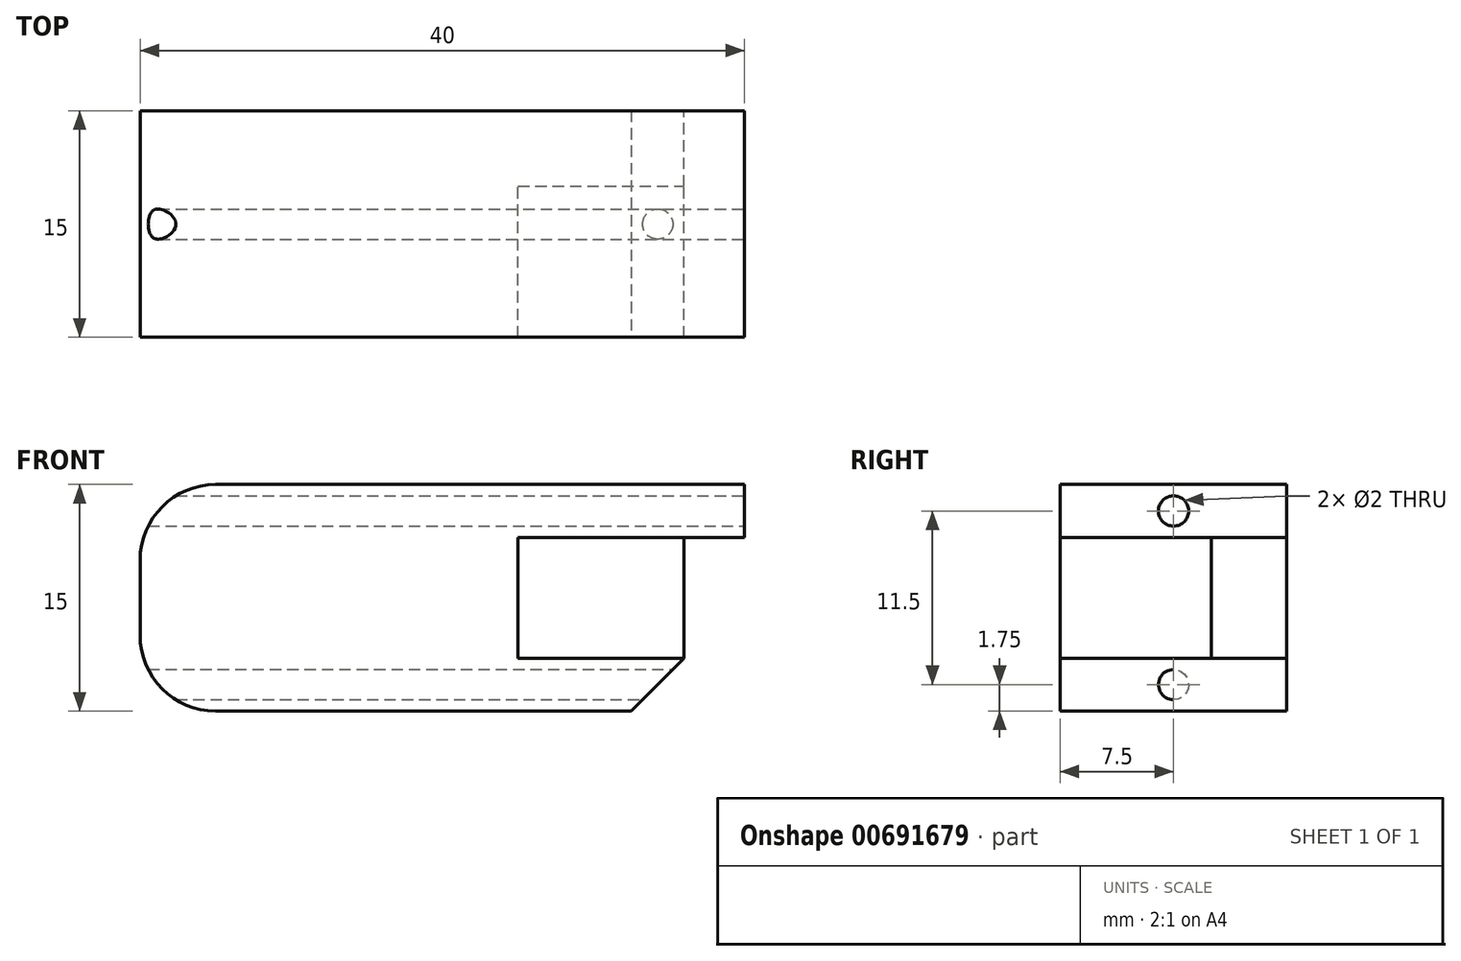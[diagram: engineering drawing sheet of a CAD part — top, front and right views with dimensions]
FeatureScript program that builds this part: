
annotation { "Feature Type Name" : "Feature", "Feature Type Description" : "" }
export const myFeature = defineFeature(function(context is Context, id is Id, definition is map)
    precondition{}
    {
        {
            var Q0;
            Q0=qCreatedBy(makeId("Front.planeOp"),FACE);
            var sketch = newSketch(context, id + "F0", { "sketchPlane" : qUnion([Q0])});
            skLineSegment(sketch, "E0.bottom", {"start": v(5, 4) * mm, "end": v(-5, 4) * mm});
            skLineSegment(sketch, "E0.top", {"start": v(5, -4) * mm, "end": v(-5, -4) * mm});
            skLineSegment(sketch, "E0.left", {"start": v(5, 4) * mm, "end": v(5, -4) * mm});
            skLineSegment(sketch, "E0.right", {"start": v(-5, 4) * mm, "end": v(-5, -4) * mm});
            skPoint(sketch, "E0.middle", {"position": v(0, 0) * mm});
            skLineSegment(sketch, "E1.bottom", {"start": v(-5, 4) * mm, "end": v(-20, 4) * mm});
            skLineSegment(sketch, "E1.top", {"start": v(-5, -4) * mm, "end": v(-20, -4) * mm});
            skLineSegment(sketch, "E1.right", {"start": v(-20, 4) * mm, "end": v(-20, -4) * mm});
            skLineSegment(sketch, "E2.bottom", {"start": v(5, 4) * mm, "end": v(20, 4) * mm});
            skLineSegment(sketch, "E2.top", {"start": v(5, -4) * mm, "end": v(20, -4) * mm});
            skLineSegment(sketch, "E2.right", {"start": v(20, 4) * mm, "end": v(20, -4) * mm});
            skLineSegment(sketch, "E3.bottom", {"start": v(-20, 4) * mm, "end": v(20, 4) * mm});
            skLineSegment(sketch, "E3.top", {"start": v(-20, 7.5) * mm, "end": v(20, 7.5) * mm});
            skLineSegment(sketch, "E3.left", {"start": v(-20, 4) * mm, "end": v(-20, 7.5) * mm});
            skLineSegment(sketch, "E3.right", {"start": v(20, 4) * mm, "end": v(20, 7.5) * mm});
            skLineSegment(sketch, "E4.bottom", {"start": v(-16, 0) * mm, "end": v(16, 0) * mm});
            skLineSegment(sketch, "E4.top", {"start": v(-16, -7.5) * mm, "end": v(16, -7.5) * mm});
            skLineSegment(sketch, "E4.left", {"start": v(-16, 0) * mm, "end": v(-16, -7.5) * mm});
            skLineSegment(sketch, "E4.right", {"start": v(16, 0) * mm, "end": v(16, -7.5) * mm});
            skLineSegment(sketch, "E5.bottom", {"start": v(5, 4) * mm, "end": v(16, 4) * mm});
            skLineSegment(sketch, "E5.top", {"start": v(5, -4) * mm, "end": v(16, -4) * mm});
            skLineSegment(sketch, "E5.right", {"start": v(16, 4) * mm, "end": v(16, -4) * mm});
            skLineSegment(sketch, "E6.bottom", {"start": v(-5, 4) * mm, "end": v(-16, 4) * mm});
            skLineSegment(sketch, "E6.top", {"start": v(-5, -4) * mm, "end": v(-16, -4) * mm});
            skLineSegment(sketch, "E6.right", {"start": v(-16, 4) * mm, "end": v(-16, -4) * mm});
            skLineSegment(sketch, "E7.bottom", {"start": v(-20, 7.5) * mm, "end": v(-5, 7.5) * mm});
            skLineSegment(sketch, "E7.top", {"start": v(-20, -7.5) * mm, "end": v(-5, -7.5) * mm});
            skLineSegment(sketch, "E7.left", {"start": v(-20, 7.5) * mm, "end": v(-20, -7.5) * mm});
            skLineSegment(sketch, "E7.right", {"start": v(-5, 7.5) * mm, "end": v(-5, -7.5) * mm});
            skSolve(sketch);
        }
        {
            var Q0;
            {var subQ4=sQuery(id+"F0.wireOp",EDGE,"E7.top");Q0=makeQuery(id+"F0.imprint","IMPRINT",FACE,{"disambiguationData":[TD([[makeQuery(id+"F0.imprint","IMPRINT",EDGE,{"derivedFrom":subQ4}),1.0]])]});}
            var Q1;
            {var subQ7=sQuery(id+"F0.wireOp",EDGE,"E0.top");Q1=makeQuery(id+"F0.imprint","IMPRINT",FACE,{"disambiguationData":[TD([[makeQuery(id+"F0.imprint","IMPRINT",EDGE,{"derivedFrom":subQ7}),1.0]])]});}
            var Q2;
            {var subQ0=sQuery(id+"F0.wireOp",EDGE,"E3.left");Q2=makeQuery(id+"F0.imprint","IMPRINT",FACE,{"disambiguationData":[TD([[makeQuery(id+"F0.imprint","IMPRINT",EDGE,{"derivedFrom":subQ0}),-1.0]])]});}
            var Q3;
            {var subQ0=sQuery(id+"F0.wireOp",EDGE,"E7.right");var subQ5=sQuery(id+"F0.wireOp",EDGE,"E4.top");var subQ6=makeQuery(id+"F0.imprint","INTERSECT",VERTEX,{"derivedFrom":[subQ5,subQ0]});Q3=makeQuery(id+"F0.imprint","IMPRINT",FACE,{"disambiguationData":[TD([[makeQuery(id+"F0.imprint","IMPRINT",EDGE,{"disambiguationData":[TD([[subQ6,1.0]])],"derivedFrom":subQ5}),1.0]])]});}
            var Q4;
            {var subQ4=sQuery(id+"F0.wireOp",EDGE,"E1.right");Q4=makeQuery(id+"F0.imprint","IMPRINT",FACE,{"disambiguationData":[TD([[makeQuery(id+"F0.imprint","IMPRINT",EDGE,{"derivedFrom":subQ4}),1.0]])]});}
            var Q5;
            {var subQ6=sQuery(id+"F0.wireOp",EDGE,"E0.bottom");Q5=makeQuery(id+"F0.imprint","IMPRINT",FACE,{"disambiguationData":[TD([[makeQuery(id+"F0.imprint","IMPRINT",EDGE,{"derivedFrom":subQ6}),-1.0]])]});}
            var Q6;
            {var subQ5=sQuery(id+"F0.wireOp",EDGE,"E6.right");Q6=makeQuery(id+"F0.imprint","IMPRINT",FACE,{"disambiguationData":[TD([[makeQuery(id+"F0.imprint","IMPRINT",EDGE,{"derivedFrom":subQ5}),1.0]])]});}
            var Q7;
            {var subQ0=sQuery(id+"F0.wireOp",EDGE,"E0.bottom");Q7=makeQuery(id+"F0.imprint","IMPRINT",FACE,{"disambiguationData":[TD([[makeQuery(id+"F0.imprint","IMPRINT",EDGE,{"derivedFrom":subQ0}),1.0]])]});}
            var Q8;
            {var subQ1=sQuery(id+"F0.wireOp",EDGE,"E0.right");var subQ3=sQuery(id+"F0.wireOp",EDGE,"E4.bottom");var subQ4=makeQuery(id+"F0.imprint","INTERSECT",VERTEX,{"derivedFrom":[subQ1,subQ3]});Q8=makeQuery(id+"F0.imprint","IMPRINT",FACE,{"disambiguationData":[TD([[makeQuery(id+"F0.imprint","IMPRINT",EDGE,{"disambiguationData":[TD([[subQ4,1.0]])],"derivedFrom":subQ3}),-1.0]])]});}
            var Q9;
            {var subQ0=sQuery(id+"F0.wireOp",EDGE,"E0.top");Q9=makeQuery(id+"F0.imprint","IMPRINT",FACE,{"disambiguationData":[TD([[makeQuery(id+"F0.imprint","IMPRINT",EDGE,{"derivedFrom":subQ0}),-1.0]])]});}
            extrude(context, id + "F1", {"entities" : qUnion([Q0, Q1, Q2, Q3, Q4, Q5, Q6, Q7, Q8, Q9]), "depth" : 15 * mm, "offsetDistance" : 25 * mm});
        }
        {
            var Q0;
            {var subQ5=sQuery(id+"F0.wireOp",EDGE,"E6.right");Q0=makeQuery(id+"F0.imprint","IMPRINT",FACE,{"disambiguationData":[TD([[makeQuery(id+"F0.imprint","IMPRINT",EDGE,{"derivedFrom":subQ5}),1.0]])]});}
            var Q1;
            {var subQ0=sQuery(id+"F0.wireOp",EDGE,"E0.bottom");Q1=makeQuery(id+"F0.imprint","IMPRINT",FACE,{"disambiguationData":[TD([[makeQuery(id+"F0.imprint","IMPRINT",EDGE,{"derivedFrom":subQ0}),1.0]])]});}
            var Q2;
            {var subQ0=sQuery(id+"F0.wireOp",EDGE,"E0.top");Q2=makeQuery(id+"F0.imprint","IMPRINT",FACE,{"disambiguationData":[TD([[makeQuery(id+"F0.imprint","IMPRINT",EDGE,{"derivedFrom":subQ0}),-1.0]])]});}
            var Q3;
            {var subQ5=sQuery(id+"F0.wireOp",EDGE,"E5.right");Q3=makeQuery(id+"F0.imprint","IMPRINT",FACE,{"disambiguationData":[TD([[makeQuery(id+"F0.imprint","IMPRINT",EDGE,{"derivedFrom":subQ5}),-1.0]])]});}
            var Q4;
            {var subQ1=sQuery(id+"F0.wireOp",EDGE,"E0.right");var subQ3=sQuery(id+"F0.wireOp",EDGE,"E4.bottom");var subQ4=makeQuery(id+"F0.imprint","INTERSECT",VERTEX,{"derivedFrom":[subQ1,subQ3]});Q4=makeQuery(id+"F0.imprint","IMPRINT",FACE,{"disambiguationData":[TD([[makeQuery(id+"F0.imprint","IMPRINT",EDGE,{"disambiguationData":[TD([[subQ4,1.0]])],"derivedFrom":subQ3}),-1.0]])]});}
            var Q5;
            {var subQ1=sQuery(id+"F0.wireOp",EDGE,"E0.left");var subQ3=sQuery(id+"F0.wireOp",EDGE,"E4.bottom");var subQ4=makeQuery(id+"F0.imprint","INTERSECT",VERTEX,{"derivedFrom":[subQ1,subQ3]});Q5=makeQuery(id+"F0.imprint","IMPRINT",FACE,{"disambiguationData":[TD([[makeQuery(id+"F0.imprint","IMPRINT",EDGE,{"disambiguationData":[TD([[subQ4,-1.0]])],"derivedFrom":subQ1}),1.0]])]});}
            var Q6;
            {var subQ6=sQuery(id+"F0.wireOp",EDGE,"E0.bottom");Q6=makeQuery(id+"F0.imprint","IMPRINT",FACE,{"disambiguationData":[TD([[makeQuery(id+"F0.imprint","IMPRINT",EDGE,{"derivedFrom":subQ6}),-1.0]])]});}
            var Q7;
            {var subQ7=sQuery(id+"F0.wireOp",EDGE,"E0.top");Q7=makeQuery(id+"F0.imprint","IMPRINT",FACE,{"disambiguationData":[TD([[makeQuery(id+"F0.imprint","IMPRINT",EDGE,{"derivedFrom":subQ7}),1.0]])]});}
            var Q8;
            {var subQ0=sQuery(id+"F0.wireOp",EDGE,"E7.right");var subQ5=sQuery(id+"F0.wireOp",EDGE,"E4.top");var subQ6=makeQuery(id+"F0.imprint","INTERSECT",VERTEX,{"derivedFrom":[subQ5,subQ0]});Q8=makeQuery(id+"F0.imprint","IMPRINT",FACE,{"disambiguationData":[TD([[makeQuery(id+"F0.imprint","IMPRINT",EDGE,{"disambiguationData":[TD([[subQ6,1.0]])],"derivedFrom":subQ5}),1.0]])]});}
            var Q9;
            {var subQ4=sQuery(id+"F0.wireOp",EDGE,"E7.top");Q9=makeQuery(id+"F0.imprint","IMPRINT",FACE,{"disambiguationData":[TD([[makeQuery(id+"F0.imprint","IMPRINT",EDGE,{"derivedFrom":subQ4}),1.0]])]});}
            var Q10;
            {var subQ4=sQuery(id+"F0.wireOp",EDGE,"E1.right");Q10=makeQuery(id+"F0.imprint","IMPRINT",FACE,{"disambiguationData":[TD([[makeQuery(id+"F0.imprint","IMPRINT",EDGE,{"derivedFrom":subQ4}),1.0]])]});}
            var Q11;
            {var subQ0=sQuery(id+"F0.wireOp",EDGE,"E3.left");Q11=makeQuery(id+"F0.imprint","IMPRINT",FACE,{"disambiguationData":[TD([[makeQuery(id+"F0.imprint","IMPRINT",EDGE,{"derivedFrom":subQ0}),-1.0]])]});}
            extrude(context, id + "F2", {"entities" : qUnion([Q0, Q1, Q2, Q3, Q4, Q5, Q6, Q7, Q8, Q9, Q10, Q11]), "operationType" : NewBodyOperationType.ADD, "depth" : 5 * mm, "offsetDistance" : 25 * mm});
        }
        {
            var Q0;
            Q0=makeQuery(id+"F1.opExtrude","SWEPT_EDGE",EDGE,{"disambiguationData":[OSD([sQuery(id+"F0.wireOp",EDGE,"E3.top"),sQuery(id+"F0.wireOp",EDGE,"E3.left")])]});
            fillet(context, id + "F3", {"entities" : qUnion([Q0]), "radius" : 5 * mm, "tangentPropagation" : true, "allowEdgeOverflow" : false});
        }
        {
            var Q0;
            Q0=makeQuery(id+"F1.opExtrude","SWEPT_EDGE",EDGE,{"disambiguationData":[OSD([sQuery(id+"F0.wireOp",EDGE,"E7.top"),sQuery(id+"F0.wireOp",EDGE,"E7.left")])]});
            fillet(context, id + "F4", {"entities" : qUnion([Q0]), "radius" : 5 * mm, "tangentPropagation" : true, "allowEdgeOverflow" : false});
        }
        {
            var Q0;
            Q0=makeQuery(id+"F1.opExtrude","SWEPT_EDGE",EDGE,{"disambiguationData":[OSD([sQuery(id+"F0.wireOp",EDGE,"E4.top"),sQuery(id+"F0.wireOp",EDGE,"E4.right")])]});
            chamfer(context, id + "F5", {"entities" : qUnion([Q0]), "width" : 3.5 * mm, "tangentPropagation" : true});
        }
        {
            var Q0;
            Q0=makeQuery(id+"F1.opExtrude","SWEPT_FACE",FACE,{"disambiguationData":[OSD([sQuery(id+"F0.wireOp",EDGE,"E3.right")])]});
            var sketch = newSketch(context, id + "F6", { "sketchPlane" : qUnion([Q0])});
            skLineSegment(sketch, "E8", {"start": v(-7.5, 7.5) * mm, "end": v(-7.5, -7.5) * mm});
            skLineSegment(sketch, "E9", {"start": v(-7.5, 7.5) * mm, "end": v(-7.5, 4) * mm});
            skLineSegment(sketch, "E10", {"start": v(-7.5, -7.5) * mm, "end": v(-7.5, -4) * mm});
            skCircle(sketch, "E11", {"center": v(-7.5, -5.75) * mm, "radius": 1 * mm});
            skCircle(sketch, "E12", {"center": v(-7.5, 5.75) * mm, "radius": 1 * mm});
            skPoint(sketch, "E12.perimeterSnap0", {"position": v(-7.5, 5.75) * mm});
            skSolve(sketch);
        }
        {
            var Q0;
            Q0 = qSketchRegion(id + "F6", true);
            extrude(context, id + "F7", {"entities" : qUnion([Q0]), "operationType" : NewBodyOperationType.REMOVE, "oppositeDirection" : true, "depth" : 40 * mm, "offsetDistance" : 25 * mm});
        }
    });
